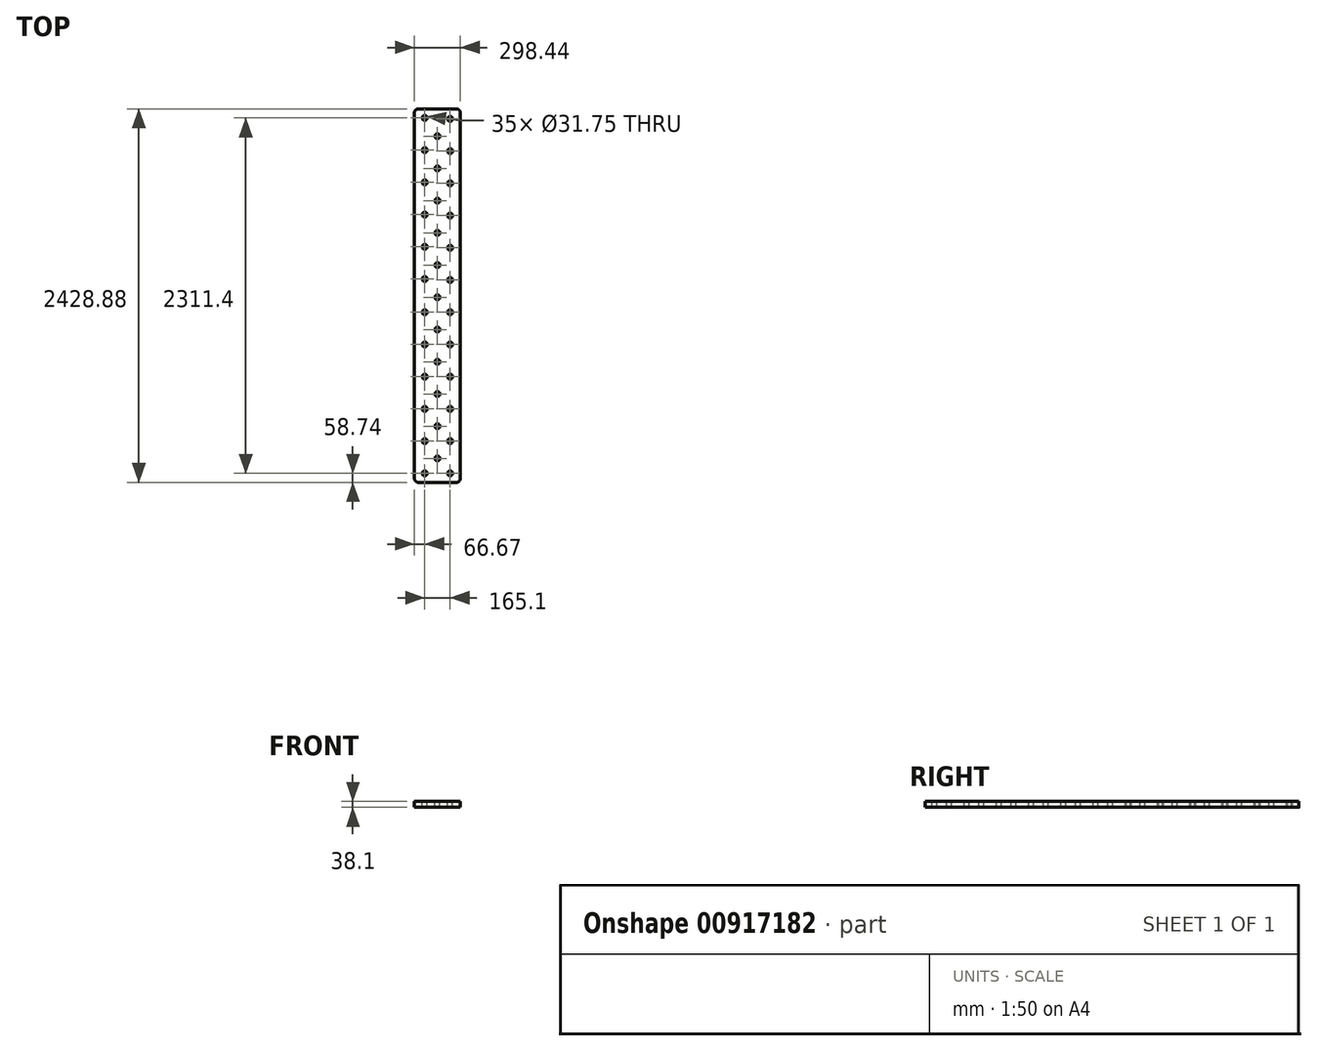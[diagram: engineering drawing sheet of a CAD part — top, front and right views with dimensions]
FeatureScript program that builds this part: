
annotation { "Feature Type Name" : "Feature", "Feature Type Description" : "" }
export const myFeature = defineFeature(function(context is Context, id is Id, definition is map)
    precondition{}
    {
        {
            var Q0;
            Q0=qCreatedBy(makeId("Top.planeOp"),FACE);
            var sketch = newSketch(context, id + "F0", { "sketchPlane" : qUnion([Q0])});
            skLineSegment(sketch, "E0.bottom", {"start": v(149.22, 1214.44) * mm, "end": v(-149.23, 1214.44) * mm});
            skLineSegment(sketch, "E0.top", {"start": v(149.23, -1214.44) * mm, "end": v(-149.22, -1214.44) * mm});
            skLineSegment(sketch, "E0.left", {"start": v(149.22, 1214.44) * mm, "end": v(149.23, -1214.44) * mm});
            skLineSegment(sketch, "E0.right", {"start": v(-149.23, 1214.44) * mm, "end": v(-149.22, -1214.44) * mm});
            skPoint(sketch, "E0.middle", {"position": v(0, 0) * mm});
            skSolve(sketch);
        }
        {
            var Q0;
            Q0 = qSketchRegion(id + "F0", true);
            extrude(context, id + "F1", {"entities" : qUnion([Q0]), "depth" : 38.1 * mm, "offsetDistance" : 25.4 * mm});
        }
        {
            var Q0;
            Q0=makeQuery(id+"F1.opExtrude","SWEPT_EDGE",EDGE,{"disambiguationData":[OSD([sQuery(id+"F0.wireOp",EDGE,"E0.bottom"),sQuery(id+"F0.wireOp",EDGE,"E0.left")])]});
            fillet(context, id + "F2", {"entities" : qUnion([Q0]), "radius" : 25.4 * mm, "tangentPropagation" : true, "allowEdgeOverflow" : false});
        }
        {
            var Q0;
            Q0=makeQuery(id+"F1.opExtrude","SWEPT_EDGE",EDGE,{"disambiguationData":[OSD([sQuery(id+"F0.wireOp",EDGE,"E0.bottom"),sQuery(id+"F0.wireOp",EDGE,"E0.right")])]});
            fillet(context, id + "F3", {"entities" : qUnion([Q0]), "radius" : 25.4 * mm, "tangentPropagation" : true, "allowEdgeOverflow" : false});
        }
        {
            var Q0;
            Q0=makeQuery(id+"F1.opExtrude","SWEPT_EDGE",EDGE,{"disambiguationData":[OSD([sQuery(id+"F0.wireOp",EDGE,"E0.top"),sQuery(id+"F0.wireOp",EDGE,"E0.right")])]});
            var Q1;
            Q1=makeQuery(id+"F1.opExtrude","SWEPT_EDGE",EDGE,{"disambiguationData":[OSD([sQuery(id+"F0.wireOp",EDGE,"E0.top"),sQuery(id+"F0.wireOp",EDGE,"E0.left")])]});
            fillet(context, id + "F4", {"entities" : qUnion([Q0, Q1]), "radius" : 25.4 * mm, "tangentPropagation" : true, "allowEdgeOverflow" : false});
        }
        {
            var Q0;
            Q0=makeQuery(id+"F1.opExtrude","CAP_FACE",FACE,{"disambiguationData":[OSD([sQuery(id+"F0.wireOp",EDGE,"E0.bottom"),sQuery(id+"F0.wireOp",EDGE,"E0.top"),sQuery(id+"F0.wireOp",EDGE,"E0.left"),sQuery(id+"F0.wireOp",EDGE,"E0.right")])],"isStart":false});
            var sketch = newSketch(context, id + "F5", { "sketchPlane" : qUnion([Q0])});
            skCircle(sketch, "E1", {"center": v(-82.55, -1155.7) * mm, "radius": 15.88 * mm});
            skCircle(sketch, "E2", {"center": v(82.55, -1155.7) * mm, "radius": 15.88 * mm});
            skCircle(sketch, "E3", {"center": v(0, -1058.86) * mm, "radius": 15.88 * mm});
            skCircle(sketch, "E4", {"center": v(-82.55, -946.15) * mm, "radius": 15.88 * mm});
            skCircle(sketch, "E5", {"center": v(82.55, -946.15) * mm, "radius": 15.88 * mm});
            skCircle(sketch, "E6", {"center": v(0, -849.31) * mm, "radius": 15.88 * mm});
            skCircle(sketch, "E7", {"center": v(-82.55, -736.6) * mm, "radius": 15.88 * mm});
            skCircle(sketch, "E8", {"center": v(82.55, -736.6) * mm, "radius": 15.88 * mm});
            skCircle(sketch, "E9", {"center": v(0, -639.76) * mm, "radius": 15.88 * mm});
            skCircle(sketch, "E10", {"center": v(82.55, -527.05) * mm, "radius": 15.88 * mm});
            skCircle(sketch, "E11", {"center": v(-82.55, -527.05) * mm, "radius": 15.88 * mm});
            skCircle(sketch, "E12", {"center": v(-82.55, -317.5) * mm, "radius": 15.88 * mm});
            skCircle(sketch, "E13", {"center": v(0, -430.21) * mm, "radius": 15.88 * mm});
            skCircle(sketch, "E14", {"center": v(82.55, -317.5) * mm, "radius": 15.88 * mm});
            skCircle(sketch, "E15", {"center": v(0, -220.66) * mm, "radius": 15.88 * mm});
            skCircle(sketch, "E16", {"center": v(-82.55, -107.95) * mm, "radius": 15.88 * mm});
            skCircle(sketch, "E17", {"center": v(82.55, -107.95) * mm, "radius": 15.88 * mm});
            skCircle(sketch, "E18", {"center": v(0, -11.11) * mm, "radius": 15.88 * mm});
            skCircle(sketch, "E19", {"center": v(82.55, 101.6) * mm, "radius": 15.88 * mm});
            skCircle(sketch, "E20", {"center": v(-82.55, 107.95) * mm, "radius": 15.88 * mm});
            skCircle(sketch, "E21", {"center": v(0, 198.44) * mm, "radius": 15.88 * mm});
            skCircle(sketch, "E22", {"center": v(-82.55, 317.5) * mm, "radius": 15.88 * mm});
            skCircle(sketch, "E23", {"center": v(82.55, 311.15) * mm, "radius": 15.88 * mm});
            skCircle(sketch, "E24", {"center": v(0, 407.99) * mm, "radius": 15.88 * mm});
            skCircle(sketch, "E25", {"center": v(82.55, 520.7) * mm, "radius": 15.88 * mm});
            skCircle(sketch, "E26", {"center": v(-82.55, 527.05) * mm, "radius": 15.88 * mm});
            skCircle(sketch, "E27", {"center": v(0, 617.54) * mm, "radius": 15.88 * mm});
            skCircle(sketch, "E28", {"center": v(-82.55, 736.6) * mm, "radius": 15.88 * mm});
            skCircle(sketch, "E29", {"center": v(82.55, 730.25) * mm, "radius": 15.88 * mm});
            skCircle(sketch, "E30", {"center": v(0, 827.09) * mm, "radius": 15.88 * mm});
            skCircle(sketch, "E31", {"center": v(-82.55, 946.15) * mm, "radius": 15.88 * mm});
            skCircle(sketch, "E32", {"center": v(82.55, 939.8) * mm, "radius": 15.88 * mm});
            skCircle(sketch, "E33", {"center": v(0, 1036.64) * mm, "radius": 15.88 * mm});
            skCircle(sketch, "E34", {"center": v(-82.55, 1155.7) * mm, "radius": 15.88 * mm});
            skCircle(sketch, "E35", {"center": v(82.55, 1149.35) * mm, "radius": 15.88 * mm});
            skSolve(sketch);
        }
        {
            var Q0;
            Q0=sQuery(id+"F5.wireOp",VERTEX,"E1.center");
            var Q1;
            Q1=sQuery(id+"F5.wireOp",VERTEX,"E2.center");
            var Q2;
            Q2=sQuery(id+"F5.wireOp",VERTEX,"E3.center");
            var Q3;
            Q3=sQuery(id+"F5.wireOp",VERTEX,"E5.center");
            var Q4;
            Q4=sQuery(id+"F5.wireOp",VERTEX,"E4.center");
            var Q5;
            Q5=sQuery(id+"F5.wireOp",VERTEX,"E33.center");
            var Q6;
            Q6=sQuery(id+"F5.wireOp",VERTEX,"E35.center");
            var Q7;
            Q7=sQuery(id+"F5.wireOp",VERTEX,"E32.center");
            var Q8;
            Q8=sQuery(id+"F5.wireOp",VERTEX,"E34.center");
            var Q9;
            Q9=sQuery(id+"F5.wireOp",VERTEX,"E31.center");
            var Q10;
            Q10=sQuery(id+"F5.wireOp",VERTEX,"E30.center");
            var Q11;
            Q11=sQuery(id+"F5.wireOp",VERTEX,"E29.center");
            var Q12;
            Q12=sQuery(id+"F5.wireOp",VERTEX,"E28.center");
            var Q13;
            Q13=sQuery(id+"F5.wireOp",VERTEX,"E27.center");
            var Q14;
            Q14=sQuery(id+"F5.wireOp",VERTEX,"E25.center");
            var Q15;
            Q15=sQuery(id+"F5.wireOp",VERTEX,"E22.center");
            var Q16;
            Q16=sQuery(id+"F5.wireOp",VERTEX,"E24.center");
            var Q17;
            Q17=sQuery(id+"F5.wireOp",VERTEX,"E26.center");
            var Q18;
            Q18=sQuery(id+"F5.wireOp",VERTEX,"E23.center");
            var Q19;
            Q19=sQuery(id+"F5.wireOp",VERTEX,"E21.center");
            var Q20;
            Q20=sQuery(id+"F5.wireOp",VERTEX,"E18.center");
            var Q21;
            Q21=sQuery(id+"F5.wireOp",VERTEX,"E20.center");
            var Q22;
            Q22=sQuery(id+"F5.wireOp",VERTEX,"E19.center");
            var Q23;
            Q23=sQuery(id+"F5.wireOp",VERTEX,"E16.center");
            var Q24;
            Q24=sQuery(id+"F5.wireOp",VERTEX,"E17.center");
            var Q25;
            Q25=sQuery(id+"F5.wireOp",VERTEX,"E15.center");
            var Q26;
            Q26=sQuery(id+"F5.wireOp",VERTEX,"E12.center");
            var Q27;
            Q27=sQuery(id+"F5.wireOp",VERTEX,"E13.center");
            var Q28;
            Q28=sQuery(id+"F5.wireOp",VERTEX,"E14.center");
            var Q29;
            Q29=sQuery(id+"F5.wireOp",VERTEX,"E10.center");
            var Q30;
            Q30=sQuery(id+"F5.wireOp",VERTEX,"E8.center");
            var Q31;
            Q31=sQuery(id+"F5.wireOp",VERTEX,"E6.center");
            var Q32;
            Q32=sQuery(id+"F5.wireOp",VERTEX,"E7.center");
            var Q33;
            Q33=sQuery(id+"F5.wireOp",VERTEX,"E9.center");
            var Q34;
            Q34=sQuery(id+"F5.wireOp",VERTEX,"E11.center");
            var Q35;
            Q35=makeQuery(id+"F1.opExtrude","SWEPT_BODY",BODY,{"disambiguationData":[OSD([sQuery(id+"F0.wireOp",EDGE,"E0.bottom"),sQuery(id+"F0.wireOp",EDGE,"E0.top"),sQuery(id+"F0.wireOp",EDGE,"E0.left"),sQuery(id+"F0.wireOp",EDGE,"E0.right")])]});
            hole(context, id + "F6", {"style" : HoleStyle.SIMPLE, "endStyle" : HoleEndStyle.THROUGH, "holeDiameter" : 31.75 * mm, "majorDiameter" : 6.35 * mm, "isTappedThrough" : true, "tappedDepth" : 12.7 * mm, "tapClearance" : 3, "locations" : qUnion([Q0, Q1, Q2, Q3, Q4, Q5, Q6, Q7, Q8, Q9, Q10, Q11, Q12, Q13, Q14, Q15, Q16, Q17, Q18, Q19, Q20, Q21, Q22, Q23, Q24, Q25, Q26, Q27, Q28, Q29, Q30, Q31, Q32, Q33, Q34]), "scope" : qUnion([Q35])});
        }
    });
